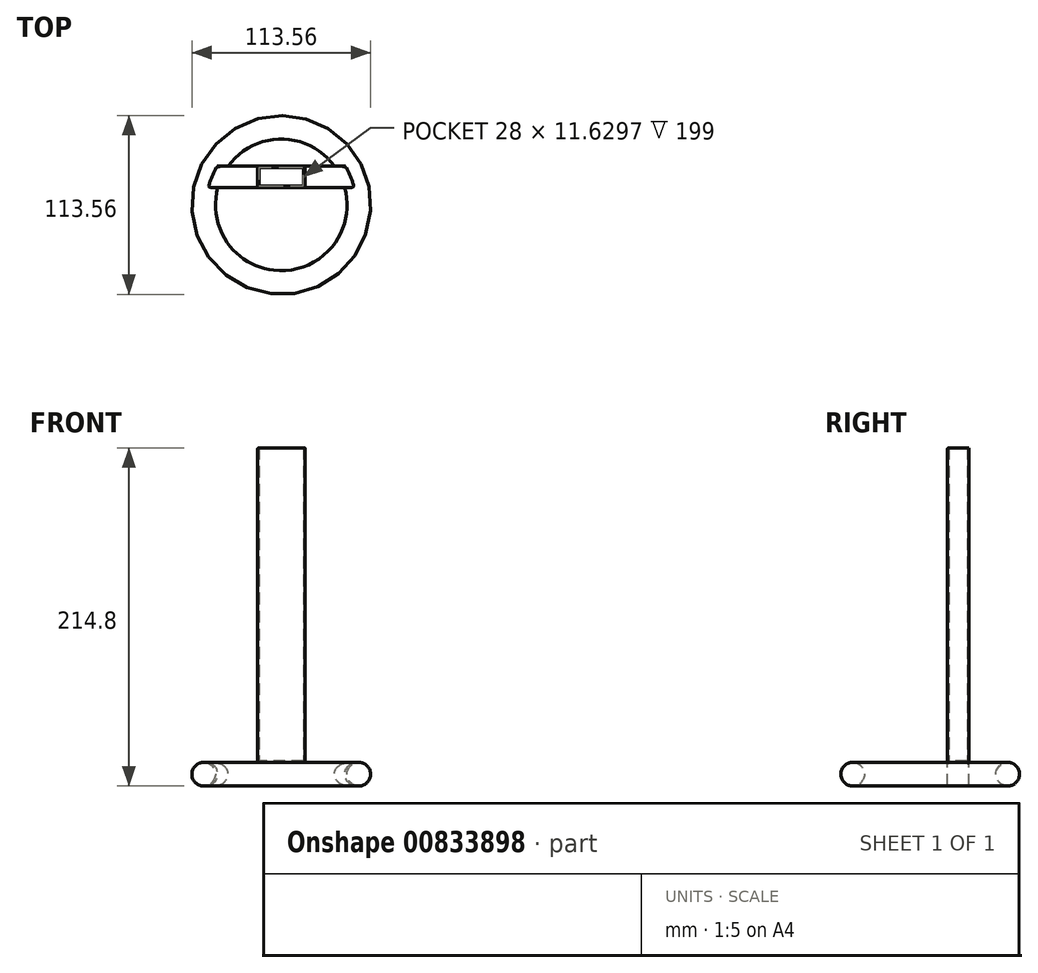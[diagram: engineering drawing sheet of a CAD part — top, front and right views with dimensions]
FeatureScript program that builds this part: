
annotation { "Feature Type Name" : "Feature", "Feature Type Description" : "" }
export const myFeature = defineFeature(function(context is Context, id is Id, definition is map)
    precondition{}
    {
        {
            var Q0;
            Q0=qCreatedBy(makeId("Top.planeOp"),FACE);
            var sketch = newSketch(context, id + "F0", { "sketchPlane" : qUnion([Q0])});
            skCircle(sketch, "E0", {"center": v(0, 0) * mm, "radius": 50 * mm});
            skSolve(sketch);
        }
        {
            var Q0;
            Q0=qCreatedBy(makeId("Front.planeOp"),FACE);
            var sketch = newSketch(context, id + "F1", { "sketchPlane" : qUnion([Q0])});
            skCircle(sketch, "E1", {"center": v(-49.28, 0) * mm, "radius": 7.5 * mm});
            skSolve(sketch);
        }
        {
            var Q0;
            Q0=makeQuery(id+"F1.imprint","IMPRINT",FACE,{"disambiguationData":[TD([[makeQuery(id+"F1.imprint","IMPRINT",EDGE,{"derivedFrom":sQuery(id+"F1.wireOp",EDGE,"E1")}),1.0]])]});
            var Q1;
            Q1=sQuery(id+"F0.wireOp",EDGE,"E0");
            sweep(context, id + "F2", {"profiles" : qUnion([Q0]), "path" : qUnion([Q1])});
        }
        {
            var Q0;
            Q0=qCreatedBy(makeId("Right.planeOp"),FACE);
            var sketch = newSketch(context, id + "F3", { "sketchPlane" : qUnion([Q0])});
            skLineSegment(sketch, "E2.bottom", {"start": v(10.95, 7.3) * mm, "end": v(24.58, 7.3) * mm});
            skLineSegment(sketch, "E2.top", {"start": v(10.95, -7.3) * mm, "end": v(24.58, -7.3) * mm});
            skLineSegment(sketch, "E2.left", {"start": v(10.95, 7.3) * mm, "end": v(10.95, -7.3) * mm});
            skLineSegment(sketch, "E2.right", {"start": v(24.58, 7.3) * mm, "end": v(24.58, -7.3) * mm});
            skSolve(sketch);
        }
        {
            var Q0;
            Q0=makeQuery(id+"F3.imprint","IMPRINT",FACE,{"disambiguationData":[TD([[makeQuery(id+"F3.imprint","IMPRINT",EDGE,{"derivedFrom":sQuery(id+"F3.wireOp",EDGE,"E2.bottom")}),-1.0]])]});
            extrude(context, id + "F4", {"entities" : qUnion([Q0]), "operationType" : NewBodyOperationType.ADD, "endBound" : BoundingType.UP_TO_NEXT, "depth" : 25 * mm, "offsetDistance" : 25 * mm});
        }
        {
            var Q0;
            Q0 = qSketchRegion(id + "F3", true);
            extrude(context, id + "F5", {"entities" : qUnion([Q0]), "operationType" : NewBodyOperationType.ADD, "endBound" : BoundingType.UP_TO_NEXT, "oppositeDirection" : true, "depth" : 25 * mm, "offsetDistance" : 25 * mm});
        }
        {
            var Q0;
            {var subQ0=sQuery(id+"F3.wireOp",EDGE,"E2.bottom");Q0=makeQuery(id+"F5.boolean.opBoolean","MERGE",FACE,{"derivedFrom":[makeQuery(id+"F4.opExtrude","SWEPT_FACE",FACE,{"disambiguationData":[OSD([subQ0])]}),makeQuery(id+"F5.opExtrude","SWEPT_FACE",FACE,{"disambiguationData":[OSD([subQ0])]})]});}
            var sketch = newSketch(context, id + "F6", { "sketchPlane" : qUnion([Q0])});
            skLineSegment(sketch, "E3.bottom", {"start": v(-15, 24.58) * mm, "end": v(15, 24.58) * mm});
            skLineSegment(sketch, "E3.top", {"start": v(-15, 10.95) * mm, "end": v(15, 10.95) * mm});
            skLineSegment(sketch, "E3.left", {"start": v(-15, 24.58) * mm, "end": v(-15, 10.95) * mm});
            skLineSegment(sketch, "E3.right", {"start": v(15, 24.58) * mm, "end": v(15, 10.95) * mm});
            skSolve(sketch);
        }
        {
            var Q0;
            Q0 = qSketchRegion(id + "F6", true);
            extrude(context, id + "F7", {"entities" : qUnion([Q0]), "depth" : 200 * mm, "offsetDistance" : 25 * mm});
        }
        {
            var Q0;
            Q0=makeQuery(id+"F7.opExtrude","CAP_FACE",FACE,{"disambiguationData":[OSD([sQuery(id+"F6.wireOp",EDGE,"E3.bottom"),sQuery(id+"F6.wireOp",EDGE,"E3.top"),sQuery(id+"F6.wireOp",EDGE,"E3.left"),sQuery(id+"F6.wireOp",EDGE,"E3.right")])],"isStart":false});
            shell(context, id + "F8", {"entities" : qUnion([Q0]), "thickness" : 1 * mm});
        }
        {
            var Q0;
            {var subQ0=sQuery(id+"F3.wireOp",EDGE,"E2.left");var subQ1=sQuery(id+"F3.wireOp",EDGE,"E2.bottom");Q0=makeQuery(id+"F5.boolean.opBoolean","MERGE",EDGE,{"derivedFrom":[makeQuery(id+"F4.opExtrude","SWEPT_EDGE",EDGE,{"disambiguationData":[OSD([subQ1,subQ0])]}),makeQuery(id+"F5.opExtrude","SWEPT_EDGE",EDGE,{"disambiguationData":[OSD([subQ1,subQ0])]})]});}
            var Q1;
            Q1=makeQuery(id+"F7.opExtrude","CAP_EDGE",EDGE,{"disambiguationData":[OSD([sQuery(id+"F6.wireOp",EDGE,"E3.right")])],"isStart":true});
            var Q2;
            Q2=makeQuery(id+"F7.opExtrude","CAP_EDGE",EDGE,{"disambiguationData":[OSD([sQuery(id+"F6.wireOp",EDGE,"E3.left")])],"isStart":true});
            var Q3;
            {var subQ0=sQuery(id+"F3.wireOp",EDGE,"E2.right");var subQ1=sQuery(id+"F3.wireOp",EDGE,"E2.bottom");Q3=makeQuery(id+"F5.boolean.opBoolean","MERGE",EDGE,{"derivedFrom":[makeQuery(id+"F4.opExtrude","SWEPT_EDGE",EDGE,{"disambiguationData":[OSD([subQ1,subQ0])]}),makeQuery(id+"F5.opExtrude","SWEPT_EDGE",EDGE,{"disambiguationData":[OSD([subQ1,subQ0])]})]});}
            var Q4;
            Q4=makeQuery(id+"F7.opExtrude","SWEPT_EDGE",EDGE,{"disambiguationData":[OSD([sQuery(id+"F3.wireOp",EDGE,"E2.bottom"),sQuery(id+"F3.wireOp",EDGE,"E2.right"),sQuery(id+"F6.wireOp",EDGE,"E3.bottom"),sQuery(id+"F6.wireOp",EDGE,"E3.left")])]});
            var Q5;
            Q5=makeQuery(id+"F7.opExtrude","SWEPT_FACE",FACE,{"disambiguationData":[OSD([sQuery(id+"F6.wireOp",EDGE,"E3.left")])]});
            var Q6;
            Q6=makeQuery(id+"F7.opExtrude","SWEPT_FACE",FACE,{"disambiguationData":[OSD([sQuery(id+"F6.wireOp",EDGE,"E3.top")])]});
            var Q7;
            Q7=makeQuery(id+"F7.opExtrude","SWEPT_EDGE",EDGE,{"disambiguationData":[OSD([sQuery(id+"F3.wireOp",EDGE,"E2.bottom"),sQuery(id+"F3.wireOp",EDGE,"E2.right"),sQuery(id+"F6.wireOp",EDGE,"E3.bottom"),sQuery(id+"F6.wireOp",EDGE,"E3.right")])]});
            var Q8;
            Q8=makeQuery(id+"F5.opExtrude","CAP_EDGE",EDGE,{"disambiguationData":[OSD([sQuery(id+"F3.wireOp",EDGE,"E2.bottom")])],"isStart":false});
            var Q9;
            Q9=makeQuery(id+"F4.opExtrude","CAP_EDGE",EDGE,{"disambiguationData":[OSD([sQuery(id+"F3.wireOp",EDGE,"E2.bottom")])],"isStart":false});
            var Q10;
            Q10=makeQuery(id+"F4.opExtrude","CAP_EDGE",EDGE,{"disambiguationData":[OSD([sQuery(id+"F3.wireOp",EDGE,"E2.left")])],"isStart":false});
            var Q11;
            Q11=makeQuery(id+"F5.opExtrude","CAP_EDGE",EDGE,{"disambiguationData":[OSD([sQuery(id+"F3.wireOp",EDGE,"E2.left")])],"isStart":false});
            var Q12;
            Q12=makeQuery(id+"F5.opExtrude","CAP_EDGE",EDGE,{"disambiguationData":[OSD([sQuery(id+"F3.wireOp",EDGE,"E2.right")])],"isStart":false});
            var Q13;
            Q13=makeQuery(id+"F4.opExtrude","CAP_EDGE",EDGE,{"disambiguationData":[OSD([sQuery(id+"F3.wireOp",EDGE,"E2.right")])],"isStart":false});
            fillet(context, id + "F9", {"entities" : qUnion([Q0, Q1, Q2, Q3, Q4, Q5, Q6, Q7, Q8, Q9, Q10, Q11, Q12, Q13]), "radius" : 1 * mm, "tangentPropagation" : true, "allowEdgeOverflow" : false});
        }
    });
